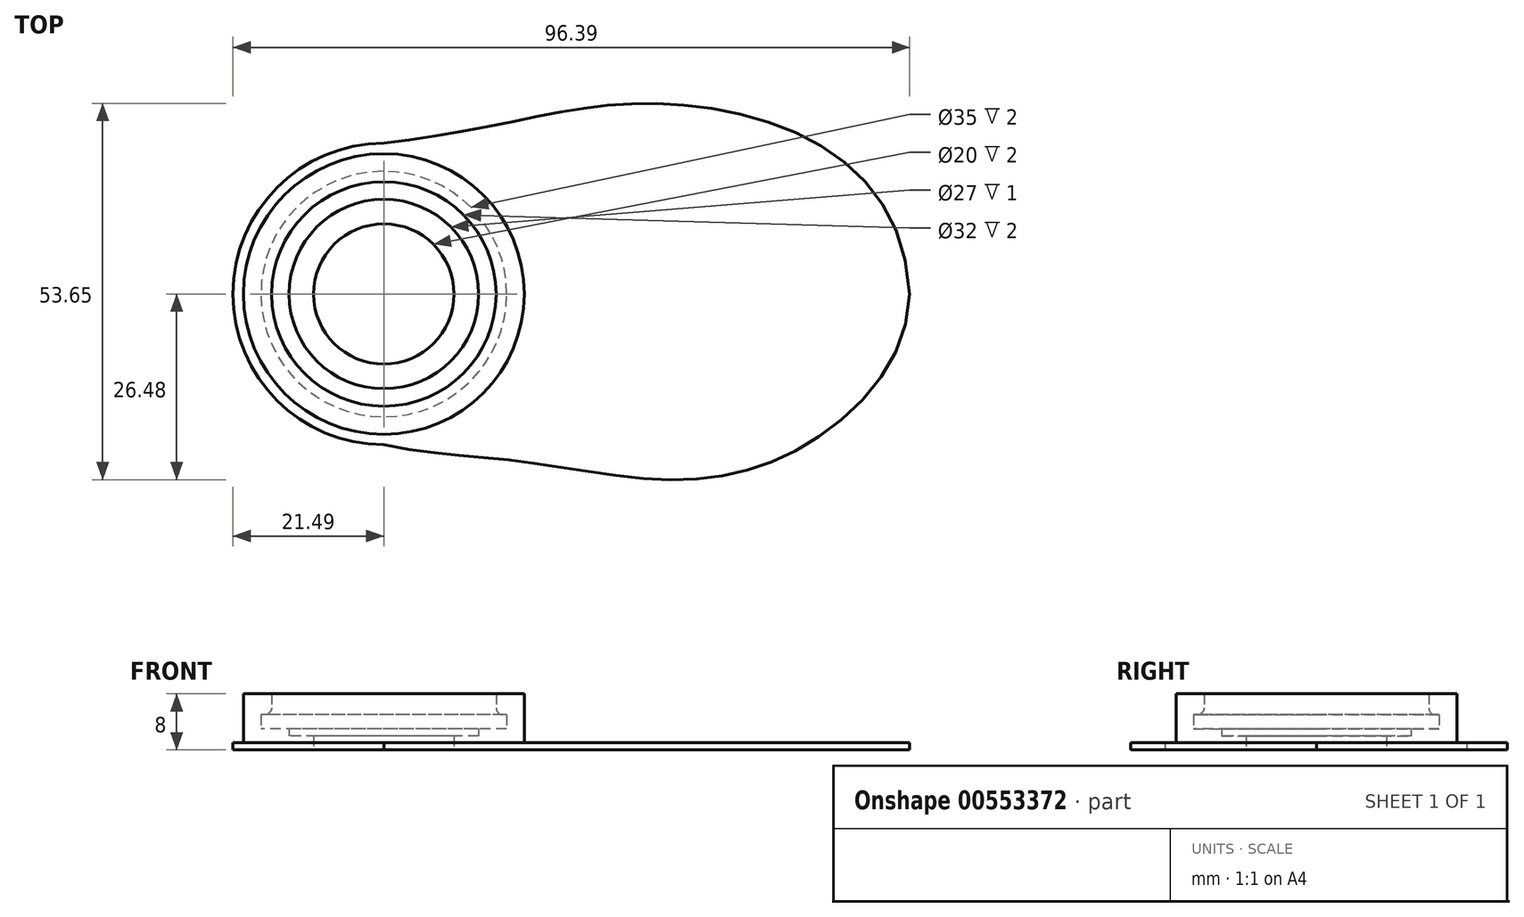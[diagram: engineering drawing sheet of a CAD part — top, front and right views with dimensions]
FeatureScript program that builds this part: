
annotation { "Feature Type Name" : "Feature", "Feature Type Description" : "" }
export const myFeature = defineFeature(function(context is Context, id is Id, definition is map)
    precondition{}
    {
        {
            var Q0;
            Q0=qCreatedBy(makeId("Top.planeOp"),FACE);
            var sketch = newSketch(context, id + "F0", { "sketchPlane" : qUnion([Q0])});
            skCircle(sketch, "E0", {"center": v(0, 0) * mm, "radius": 20 * mm});
            skCircle(sketch, "E1", {"center": v(0, 0) * mm, "radius": 10 * mm});
            skCircle(sketch, "E2", {"center": v(0, 0) * mm, "radius": 13.5 * mm});
            skCircle(sketch, "E3", {"center": v(0, 0) * mm, "radius": 17.5 * mm});
            skSolve(sketch);
        }
        {
            var Q0;
            Q0=makeQuery(id+"F0.imprint","IMPRINT",FACE,{"disambiguationData":[TD([[makeQuery(id+"F0.imprint","IMPRINT",EDGE,{"derivedFrom":sQuery(id+"F0.wireOp",EDGE,"E1")}),-1.0]])]});
            extrude(context, id + "F1", {"entities" : qUnion([Q0]), "depth" : 1 * mm, "offsetDistance" : 25 * mm});
        }
        {
            var Q0;
            Q0=makeQuery(id+"F0.imprint","IMPRINT",FACE,{"disambiguationData":[TD([[makeQuery(id+"F0.imprint","IMPRINT",EDGE,{"derivedFrom":sQuery(id+"F0.wireOp",EDGE,"E2")}),-1.0]])]});
            extrude(context, id + "F2", {"entities" : qUnion([Q0]), "operationType" : NewBodyOperationType.ADD, "depth" : 2 * mm, "offsetDistance" : 25 * mm});
        }
        {
            var Q0;
            Q0=qSketchRegion(id+"F0",true);
            extrude(context, id + "F3", {"entities" : qUnion([Q0]), "operationType" : NewBodyOperationType.ADD, "depth" : 7 * mm, "offsetDistance" : 25 * mm});
        }
        {
            var Q0;
            Q0=qCreatedBy(makeId("Top.planeOp"),FACE);
            var sketch = newSketch(context, id + "F4", { "sketchPlane" : qUnion([Q0])});
            skCircle(sketch, "E4", {"center": v(0, 0) * mm, "radius": 20 * mm});
            skCircle(sketch, "E5", {"center": v(0, 0) * mm, "radius": 16 * mm});
            skSolve(sketch);
        }
        {
            var Q0;
            Q0=qSketchRegion(id+"F4",true);
            extrude(context, id + "F5", {"entities" : qUnion([Q0]), "operationType" : NewBodyOperationType.ADD, "depth" : 7 * mm, "offsetDistance" : 25 * mm, "hasSecondDirection" : true, "secondDirectionOppositeDirection" : false, "secondDirectionDepth" : 4 * mm});
        }
        {
            var Q0;
            Q0=makeQuery(id+"F5.opExtrude","CAP_EDGE",EDGE,{"disambiguationData":[OSD([sQuery(id+"F4.wireOp",EDGE,"E5")])],"isStart":true});
            fillet(context, id + "F6", {"entities" : qUnion([Q0]), "radius" : 1 * mm, "tangentPropagation" : true, "allowEdgeOverflow" : false});
        }
        {
            var Q0;
            {var subQ0=sQuery(id+"F0.wireOp",EDGE,"E3");var subQ1=sQuery(id+"F0.wireOp",EDGE,"E2");Q0=makeQuery(id+"F3.boolean.opBoolean","MERGE",FACE,{"derivedFrom":[makeQuery(id+"F2.boolean.opBoolean","MERGE",FACE,{"derivedFrom":[makeQuery(id+"F1.opExtrude","CAP_FACE",FACE,{"disambiguationData":[OSD([sQuery(id+"F0.wireOp",EDGE,"E1"),subQ1])],"isStart":true}),makeQuery(id+"F2.opExtrude","CAP_FACE",FACE,{"disambiguationData":[OSD([subQ1,subQ0])],"isStart":true})]}),makeQuery(id+"F3.opExtrude","CAP_FACE",FACE,{"disambiguationData":[OSD([sQuery(id+"F0.wireOp",EDGE,"E0"),subQ0])],"isStart":true})]});}
            var sketch = newSketch(context, id + "F7", { "sketchPlane" : qUnion([Q0])});
            skArc(sketch, "E6", {"start": v(0, 21.49) * mm, "mid": v(-21.49, 0) * mm, "end": v(0, -21.49) * mm});
            skFitSpline(sketch, "E7", {"points": [v(0, 21.49) * mm, v(19.35, 23.83) * mm, v(42.08, 26.48) * mm, v(61.64, 20.55) * mm, v(74.9, 0) * mm], "startDerivative": vector(85.8, 18.38) * mm, "endDerivative": vector(1.78, -102.2) * mm});
            skFitSpline(sketch, "E8", {"points": [v(0, -21.49) * mm, v(20.49, -25.02) * mm, v(38.04, -27.17) * mm, v(61.64, -21.49) * mm, v(74.9, 0) * mm], "startDerivative": vector(80.85, -8.58) * mm, "endDerivative": vector(5.83, 116.63) * mm});
            skCircle(sketch, "E9", {"center": v(0, 0) * mm, "radius": 10 * mm});
            skSolve(sketch);
        }
        {
            var Q0;
            Q0 = qSketchRegion(id + "F7", true);
            extrude(context, id + "F8", {"entities" : qUnion([Q0]), "operationType" : NewBodyOperationType.ADD, "depth" : 1 * mm, "offsetDistance" : 25 * mm});
        }
    });
